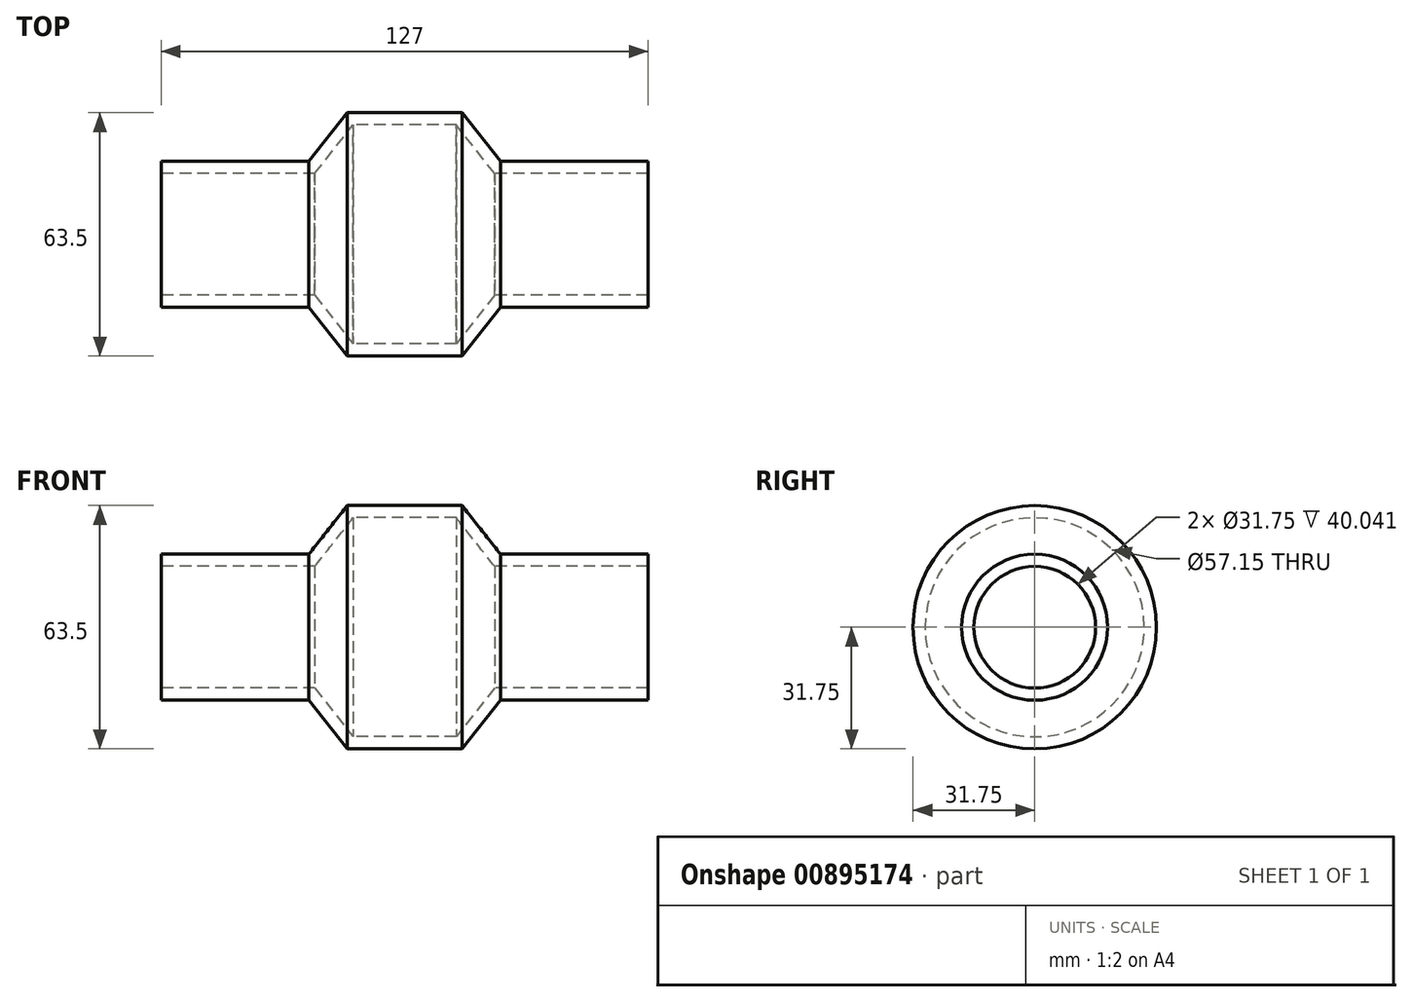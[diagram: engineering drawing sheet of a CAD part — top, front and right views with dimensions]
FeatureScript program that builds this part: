
annotation { "Feature Type Name" : "Feature", "Feature Type Description" : "" }
export const myFeature = defineFeature(function(context is Context, id is Id, definition is map)
    precondition{}
    {
        {
            var Q0;
            Q0=qCreatedBy(makeId("Front.planeOp"),FACE);
            var sketch = newSketch(context, id + "F0", { "sketchPlane" : qUnion([Q0])});
            skLineSegment(sketch, "E0", {"start": v(0, 0) * mm, "end": v(183.6, 0) * mm, "construction": true});
            skLineSegment(sketch, "E1", {"start": v(0, 15.88) * mm, "end": v(40.04, 15.88) * mm});
            skLineSegment(sketch, "E2", {"start": v(127, 15.88) * mm, "end": v(127, 19.05) * mm});
            skLineSegment(sketch, "E3", {"start": v(127, 19.05) * mm, "end": v(88.5, 19.05) * mm});
            skLineSegment(sketch, "E4", {"start": v(0, 19.05) * mm, "end": v(0, 15.88) * mm});
            skLineSegment(sketch, "E5", {"start": v(63.5, 19.05) * mm, "end": v(63.5, 61.68) * mm, "construction": true});
            skLineSegment(sketch, "E6", {"start": v(38.5, 19.05) * mm, "end": v(48.5, 31.75) * mm});
            skLineSegment(sketch, "E7", {"start": v(48.5, 31.75) * mm, "end": v(63.5, 31.75) * mm});
            skLineSegment(sketch, "E8", {"start": v(63.5, 31.75) * mm, "end": v(78.5, 31.75) * mm});
            skLineSegment(sketch, "E9", {"start": v(78.5, 31.75) * mm, "end": v(88.5, 19.05) * mm});
            skLineSegment(sketch, "E10.trimOffspring", {"start": v(38.5, 19.05) * mm, "end": v(0, 19.05) * mm});
            skLineSegment(sketch, "E11.trimOffspring", {"start": v(86.96, 15.88) * mm, "end": v(127, 15.88) * mm});
            skLineSegment(sketch, "E12", {"start": v(40.04, 15.88) * mm, "end": v(50.04, 28.58) * mm});
            skLineSegment(sketch, "E13", {"start": v(50.04, 28.57) * mm, "end": v(76.96, 28.57) * mm});
            skLineSegment(sketch, "E14", {"start": v(76.96, 28.58) * mm, "end": v(86.96, 15.87) * mm});
            skSolve(sketch);
        }
        {
            var Q0;
            Q0=qSketchRegion(id+"F0",true);
            var Q1;
            Q1=sQuery(id+"F0.wireOp",EDGE,"E0");
            revolve(context, id + "F1", {"surfaceOperationType" : NewSurfaceOperationType.NEW, "entities" : qUnion([Q0]), "axis" : qUnion([Q1]), "revolveType" : RevolveType.FULL});
        }
    });
